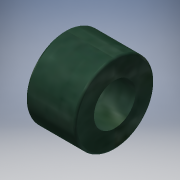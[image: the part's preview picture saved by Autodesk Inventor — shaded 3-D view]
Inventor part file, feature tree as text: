
AUTODESK INVENTOR PART (.ipt)
format: ipt  version: 2018 (Build 220112000, 112)  size: 131,584 bytes
history: native  units: mm
features: extrude x1, fillet x1, sketch x1
ambient origin geometry x8: Origin, YZ Plane, XZ Plane, XY Plane, X Axis, Y Axis, Z Axis, Center Point
bodies: Solid1 (feature_tree)
feature tree (3):
  extrude  "Extrusion1"  Depth=0.2mm
  fillet  "Fillet1"  Radius=5.0mm
  sketch  "Sketch1"  dims[d0=8.0mm d1=4.2mm d2=5.0mm d3=0.0mm d4=0.2mm]
